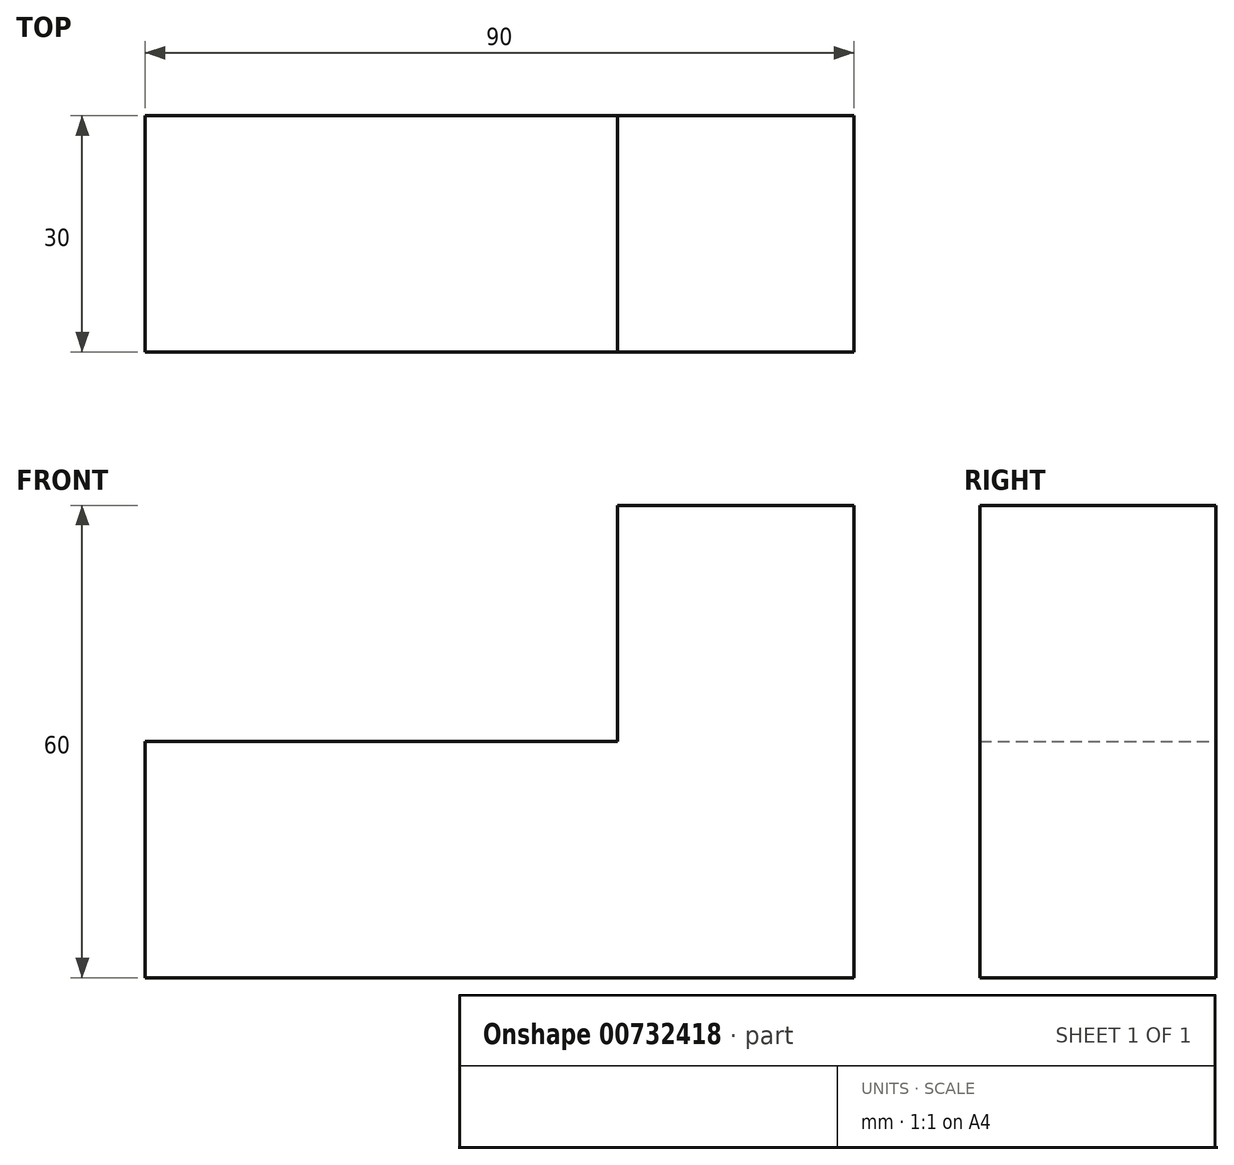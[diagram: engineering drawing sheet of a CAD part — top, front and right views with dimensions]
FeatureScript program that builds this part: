
annotation { "Feature Type Name" : "Feature", "Feature Type Description" : "" }
export const myFeature = defineFeature(function(context is Context, id is Id, definition is map)
    precondition{}
    {
        {
            var Q0;
            Q0=qCreatedBy(makeId("Front.planeOp"),FACE);
            var sketch = newSketch(context, id + "F0", { "sketchPlane" : qUnion([Q0])});
            skLineSegment(sketch, "E0", {"start": v(-90, -114.82) * mm, "end": v(0, -114.82) * mm});
            skLineSegment(sketch, "E1", {"start": v(0, -114.82) * mm, "end": v(0, -54.82) * mm});
            skLineSegment(sketch, "E2", {"start": v(0, -54.82) * mm, "end": v(-30, -54.82) * mm});
            skLineSegment(sketch, "E3", {"start": v(-30, -54.82) * mm, "end": v(-30, -84.82) * mm});
            skLineSegment(sketch, "E4", {"start": v(-30, -84.82) * mm, "end": v(-90, -84.82) * mm});
            skLineSegment(sketch, "E5", {"start": v(-90, -84.82) * mm, "end": v(-90, -114.82) * mm});
            skSolve(sketch);
        }
        {
            var Q0;
            Q0 = qSketchRegion(id + "F0", true);
            extrude(context, id + "F1", {"entities" : qUnion([Q0]), "depth" : 30 * mm, "offsetDistance" : 25 * mm});
        }
    });
